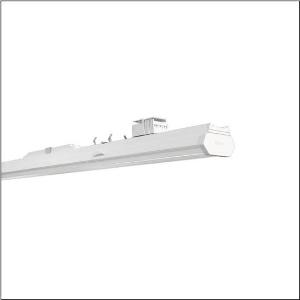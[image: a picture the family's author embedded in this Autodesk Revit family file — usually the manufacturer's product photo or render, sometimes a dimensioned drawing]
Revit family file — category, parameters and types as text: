
# Revit family: licross_r__11_protected_mo_51td12cn49xg_1fdf
name_source: partatom
category: Lighting Fixtures
units: mm (PartAtom-declared; Revit-internal decimal feet)

## family parameters
Cut with Voids When Loaded = No
Host = Face
Light Source = No
Part Type = Normal
Room Calculation Point = No
Round Connector Dimension = Use Diameter
Shared = No

## types (1)
- --- (1 x LED, 9070 lm, 49.4 W, 4000K)
    Apparent Load = 49 VA
    CIE Flux Codes = 73 92 98 99 100
    Color Rendering = 80
    Color Temperature = 4000K
    Default Elevation = 1800 mm
    Description = Licross® 11 Protected MO, luminaire insert, of sheet steel, galvanised, coil coated, white, length: 1.500mm, width: 90mm, height: 101mm, LED rated luminous flux: 9.070lm, light colour: 840, control gear: ON/OFF Multilumen, CLOi, with plug, 3-pole, with phase selection, mains connection: 220..240V, AC, 50/60Hz, start of lifetime: 49W, end of service life: 55W, halogen-free wiring, primary light control with lens, of plastic, primary optical cover: cover, of PMMA, light emission: direct distribution, primary light characteristic: symmetric, protection rating (complete): IP54, insulation class (complete): insulation class I (protective earthing), certification: CE, ENEC, VDE, UKCA, protection symbol: D if used in an environment with non-conductive dust loads with corresponding accessories, impact resistance: IK06, permissible ambient temperature for indoor applications: -35..+40°C, corresponds to IFS (International Featured Standards) requirements for safety and quality in the food industry, reducing of maximum allowable ambient temperature of 5°C with ceiling mounting, LABS conformity tested according to VDMA 24364:2018-05, packaging unit: 1 piece
    Height = 92 mm
    Lamp = 1 x LED
    Lamp Light Flux = 9070 lm
    Lamp Power = 49.4 W
    Lamp count = 1
    Length = 1500 mm
    Luminous efficacy = 184 lm/W
    Manufacturer = Siteco
    ModVariant = No
    Model = 51TD12CN49XG
    Mounting Place = Ceiling
    Mounting Type = Pendant
    Number of Poles = 1
    OnlyDefault = Yes
    Power Factor = 1
    Product Name = Licross® 11 Protected MO
    Product group = luminaire insert
    ProductGroupID = 901
    Protection Class = Protection class I
    Protection Degree = IP 54
    RLX_Detail_Level = 1
    RLX_Emergency_Light_Flux = 0 lm
    RLX_Emergency_Type = 0
    RLX_Emergency_Type_DB = No
    RlxData = <blob elided: 22081 chars, md5=6e44abd4>
    Socket = socket
    Standby Power = 0 W
    System Light Flux = 9070 lm
    System Power = 49 W
    Type Comments = factory setting: luminous flux: 100 % | (A | C | E) | 113 mA
    Type Image = l_1256145.jpg
    URL = http://relux.com
    VarID = @adj_038089
    Voltage = 0 V
    Weight = 0.00 kg
    Width = 88 mm

## geometry (parser evidence)
native form markers: Blend x4, Sweep x12
no freeform markers — native parametric forms only
